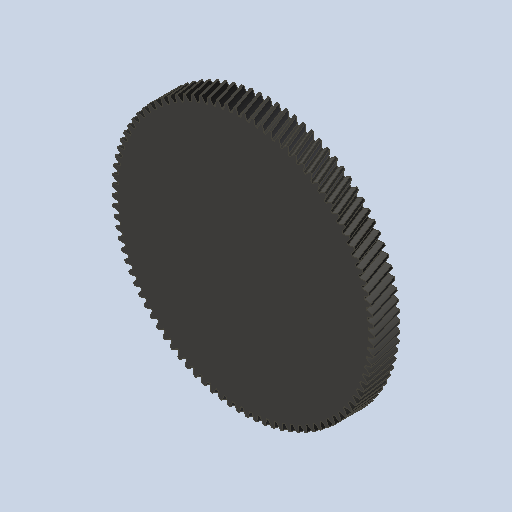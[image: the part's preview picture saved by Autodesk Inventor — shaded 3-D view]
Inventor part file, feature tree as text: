
AUTODESK INVENTOR PART (.ipt)
format: ipt  version: 2023 (Build 270158000, 158)  size: 1,126,400 bytes
history: native  units: mm (DEFAULTED — no unit token found)
features: plane x3, other x3, sketch x2, extrude x1
ambient origin geometry x8: Origin, YZ Plane, XZ Plane, XY Plane, X Axis, Y Axis, Z Axis, Center Point
bodies: Solid1 (feature_tree)
feature tree (9):
  extrude  "Extrusion1"  Depth=15.0mm TaperAngle=0.0deg
  plane  "Work Plane2"
  plane  "Work Plane8"
  plane  "Work Plane9"
  other  "Spur Gear"
  sketch  "Sketch1"  dims[d0=151.452799mm d1=15.0mm d2=0.0mm]
  sketch  "Sketch2"  dims[d3=148.452799mm d4=10.0mm d5=0.0mm d16=101.6mm d17=0.0mm d34=0.337806mm d39=0.0mm d41=0.0mm d43=101.6mm d46=101.6mm d47=0.0mm d48=0.0mm]
  other  "Srf1"
  other  "Pitch Diameter"
